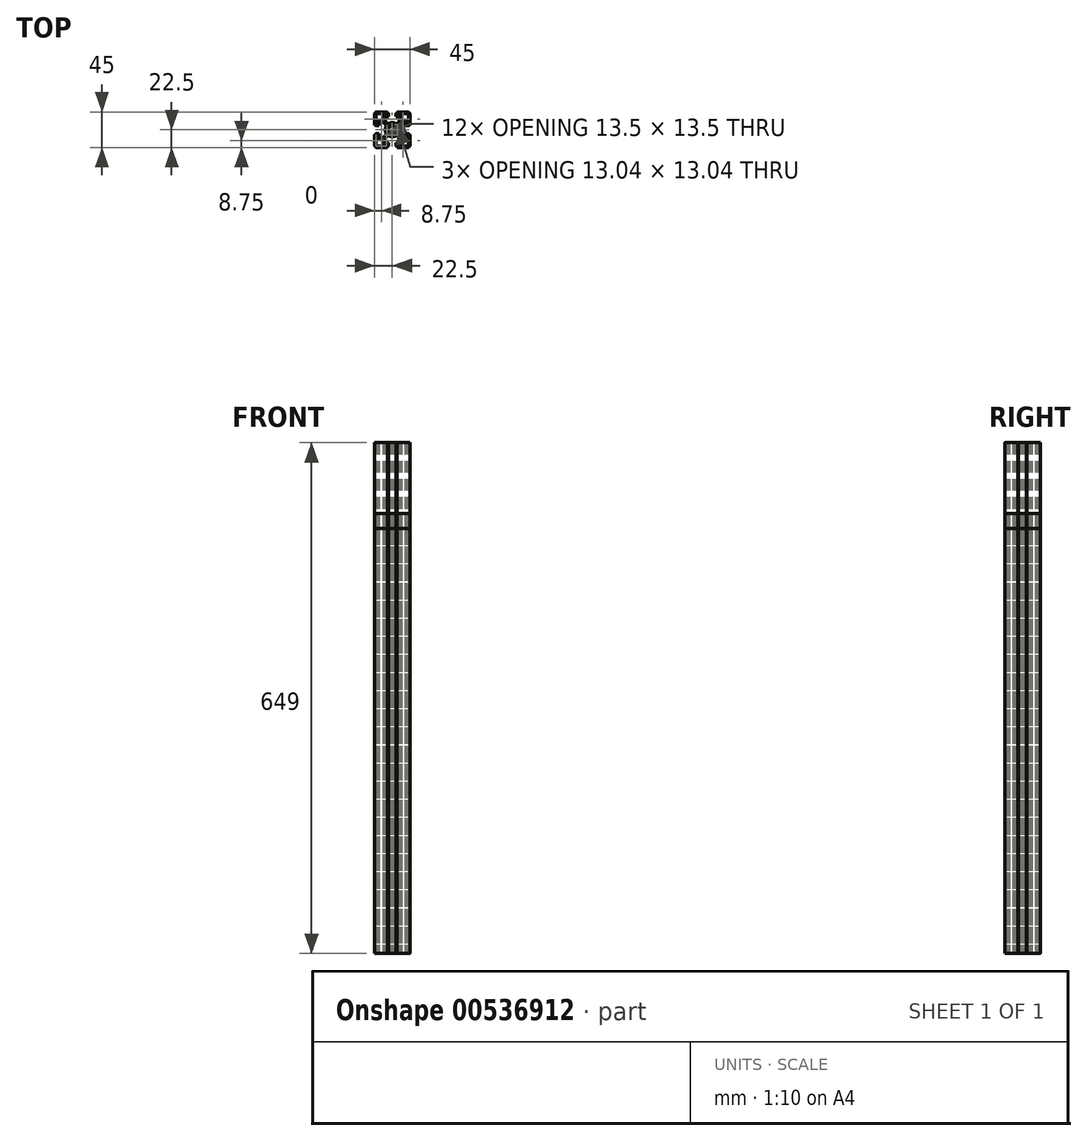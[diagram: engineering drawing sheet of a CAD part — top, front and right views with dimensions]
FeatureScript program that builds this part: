
annotation { "Feature Type Name" : "Feature", "Feature Type Description" : "" }
export const myFeature = defineFeature(function(context is Context, id is Id, definition is map)
    precondition{}
    {
        {
            var Q0;
            Q0=qCreatedBy(makeId("Top.planeOp"),FACE);
            var sketch = newSketch(context, id + "F0", { "sketchPlane" : qUnion([Q0])});
            skLineSegment(sketch, "E0.0.0", {"start": v(5, -21) * mm, "end": v(5, -16.5) * mm});
            skLineSegment(sketch, "E0.0.1", {"start": v(5, -16.5) * mm, "end": v(10, -16.5) * mm});
            skLineSegment(sketch, "E0.0.2", {"start": v(10, -16.5) * mm, "end": v(10, -11.98) * mm});
            skLineSegment(sketch, "E0.0.3", {"start": v(10, -11.98) * mm, "end": v(5.3, -7.28) * mm});
            skArc(sketch, "E0.0.4", {"start": v(5.3, -7.28) * mm, "mid": v(0, -9) * mm, "end": v(-5.3, -7.28) * mm});
            skLineSegment(sketch, "E0.0.5", {"start": v(-5.3, -7.28) * mm, "end": v(-10, -11.98) * mm});
            skLineSegment(sketch, "E0.0.6", {"start": v(-10, -11.98) * mm, "end": v(-10, -16.5) * mm});
            skLineSegment(sketch, "E0.0.7", {"start": v(-10, -16.5) * mm, "end": v(-5, -16.5) * mm});
            skLineSegment(sketch, "E0.0.8", {"start": v(-5, -16.5) * mm, "end": v(-5, -21) * mm});
            skLineSegment(sketch, "E0.0.9", {"start": v(-5, -21) * mm, "end": v(-6, -21) * mm});
            skLineSegment(sketch, "E0.0.10", {"start": v(-6, -21) * mm, "end": v(-6, -22.5) * mm});
            skLineSegment(sketch, "E0.0.11", {"start": v(-6, -22.5) * mm, "end": v(-19.5, -22.5) * mm});
            skArc(sketch, "E0.0.12", {"start": v(-19.5, -22.5) * mm, "mid": v(-21.62, -21.62) * mm, "end": v(-22.5, -19.5) * mm});
            skLineSegment(sketch, "E0.0.13", {"start": v(-22.5, -19.5) * mm, "end": v(-22.5, -6) * mm});
            skLineSegment(sketch, "E0.0.14", {"start": v(-22.5, -6) * mm, "end": v(-21, -6) * mm});
            skLineSegment(sketch, "E0.0.15", {"start": v(-21, -6) * mm, "end": v(-21, -5) * mm});
            skLineSegment(sketch, "E0.0.16", {"start": v(-21, -5) * mm, "end": v(-16.5, -5) * mm});
            skLineSegment(sketch, "E0.0.17", {"start": v(-16.5, -5) * mm, "end": v(-16.5, -10) * mm});
            skLineSegment(sketch, "E0.0.18", {"start": v(-16.5, -10) * mm, "end": v(-11.98, -10) * mm});
            skLineSegment(sketch, "E0.0.19", {"start": v(-11.98, -10) * mm, "end": v(-7.28, -5.3) * mm});
            skArc(sketch, "E0.0.20", {"start": v(-7.28, -5.3) * mm, "mid": v(-9, 0) * mm, "end": v(-7.28, 5.3) * mm});
            skLineSegment(sketch, "E0.0.21", {"start": v(-7.28, 5.3) * mm, "end": v(-11.98, 10) * mm});
            skLineSegment(sketch, "E0.0.22", {"start": v(-11.98, 10) * mm, "end": v(-16.5, 10) * mm});
            skLineSegment(sketch, "E0.0.23", {"start": v(-16.5, 10) * mm, "end": v(-16.5, 5) * mm});
            skLineSegment(sketch, "E0.0.24", {"start": v(-16.5, 5) * mm, "end": v(-21, 5) * mm});
            skLineSegment(sketch, "E0.0.25", {"start": v(-21, 5) * mm, "end": v(-21, 6) * mm});
            skLineSegment(sketch, "E0.0.26", {"start": v(-21, 6) * mm, "end": v(-22.5, 6) * mm});
            skLineSegment(sketch, "E0.0.27", {"start": v(-22.5, 6) * mm, "end": v(-22.5, 19.5) * mm});
            skArc(sketch, "E0.0.28", {"start": v(-22.5, 19.5) * mm, "mid": v(-21.62, 21.62) * mm, "end": v(-19.5, 22.5) * mm});
            skLineSegment(sketch, "E0.0.29", {"start": v(-19.5, 22.5) * mm, "end": v(-6, 22.5) * mm});
            skLineSegment(sketch, "E0.0.30", {"start": v(-6, 22.5) * mm, "end": v(-6, 21) * mm});
            skLineSegment(sketch, "E0.0.31", {"start": v(-6, 21) * mm, "end": v(-5, 21) * mm});
            skLineSegment(sketch, "E0.0.32", {"start": v(-5, 21) * mm, "end": v(-5, 16.5) * mm});
            skLineSegment(sketch, "E0.0.33", {"start": v(-5, 16.5) * mm, "end": v(-10, 16.5) * mm});
            skLineSegment(sketch, "E0.0.34", {"start": v(-10, 16.5) * mm, "end": v(-10, 11.98) * mm});
            skLineSegment(sketch, "E0.0.35", {"start": v(-10, 11.98) * mm, "end": v(-5.3, 7.28) * mm});
            skArc(sketch, "E0.0.36", {"start": v(-5.3, 7.28) * mm, "mid": v(0, 9) * mm, "end": v(5.3, 7.28) * mm});
            skLineSegment(sketch, "E0.0.37", {"start": v(5.3, 7.28) * mm, "end": v(10, 11.98) * mm});
            skLineSegment(sketch, "E0.0.38", {"start": v(10, 11.98) * mm, "end": v(10, 16.5) * mm});
            skLineSegment(sketch, "E0.0.39", {"start": v(10, 16.5) * mm, "end": v(5, 16.5) * mm});
            skLineSegment(sketch, "E0.0.40", {"start": v(5, 16.5) * mm, "end": v(5, 21) * mm});
            skLineSegment(sketch, "E0.0.41", {"start": v(5, 21) * mm, "end": v(6, 21) * mm});
            skLineSegment(sketch, "E0.0.42", {"start": v(6, 21) * mm, "end": v(6, 22.5) * mm});
            skLineSegment(sketch, "E0.0.43", {"start": v(6, 22.5) * mm, "end": v(19.5, 22.5) * mm});
            skArc(sketch, "E0.0.44", {"start": v(19.5, 22.5) * mm, "mid": v(21.62, 21.62) * mm, "end": v(22.5, 19.5) * mm});
            skLineSegment(sketch, "E0.0.45", {"start": v(22.5, 19.5) * mm, "end": v(22.5, 6) * mm});
            skLineSegment(sketch, "E0.0.46", {"start": v(22.5, 6) * mm, "end": v(21, 6) * mm});
            skLineSegment(sketch, "E0.0.47", {"start": v(21, 6) * mm, "end": v(21, 5) * mm});
            skLineSegment(sketch, "E0.0.48", {"start": v(21, 5) * mm, "end": v(16.5, 5) * mm});
            skLineSegment(sketch, "E0.0.49", {"start": v(16.5, 5) * mm, "end": v(16.5, 10) * mm});
            skLineSegment(sketch, "E0.0.50", {"start": v(16.5, 10) * mm, "end": v(11.98, 10) * mm});
            skLineSegment(sketch, "E0.0.51", {"start": v(11.98, 10) * mm, "end": v(7.28, 5.3) * mm});
            skArc(sketch, "E0.0.52", {"start": v(7.28, 5.3) * mm, "mid": v(9, 0) * mm, "end": v(7.28, -5.3) * mm});
            skLineSegment(sketch, "E0.0.53", {"start": v(7.28, -5.3) * mm, "end": v(11.98, -10) * mm});
            skLineSegment(sketch, "E0.0.54", {"start": v(11.98, -10) * mm, "end": v(16.5, -10) * mm});
            skLineSegment(sketch, "E0.0.55", {"start": v(16.5, -10) * mm, "end": v(16.5, -5) * mm});
            skLineSegment(sketch, "E0.0.56", {"start": v(16.5, -5) * mm, "end": v(21, -5) * mm});
            skLineSegment(sketch, "E0.0.57", {"start": v(21, -5) * mm, "end": v(21, -6) * mm});
            skLineSegment(sketch, "E0.0.58", {"start": v(21, -6) * mm, "end": v(22.5, -6) * mm});
            skLineSegment(sketch, "E0.0.59", {"start": v(22.5, -6) * mm, "end": v(22.5, -19.5) * mm});
            skArc(sketch, "E0.0.60", {"start": v(22.5, -19.5) * mm, "mid": v(21.62, -21.62) * mm, "end": v(19.5, -22.5) * mm});
            skLineSegment(sketch, "E0.0.61", {"start": v(19.5, -22.5) * mm, "end": v(6, -22.5) * mm});
            skLineSegment(sketch, "E0.0.62", {"start": v(6, -22.5) * mm, "end": v(6, -21) * mm});
            skLineSegment(sketch, "E0.0.63", {"start": v(6, -21) * mm, "end": v(5, -21) * mm});
            skLineSegment(sketch, "E1.0", {"start": v(11.98, 11.98) * mm, "end": v(18.5, 11.98) * mm});
            skLineSegment(sketch, "E1.1", {"start": v(18.5, 11.98) * mm, "end": v(18.5, 7) * mm});
            skLineSegment(sketch, "E1.2", {"start": v(18.5, 7) * mm, "end": v(20.5, 7) * mm});
            skLineSegment(sketch, "E1.3", {"start": v(20.5, 7) * mm, "end": v(20.5, 20.5) * mm});
            skLineSegment(sketch, "E1.4", {"start": v(20.5, 20.5) * mm, "end": v(7, 20.5) * mm});
            skLineSegment(sketch, "E1.5", {"start": v(7, 20.5) * mm, "end": v(7, 18.5) * mm});
            skLineSegment(sketch, "E1.6", {"start": v(7, 18.5) * mm, "end": v(11.98, 18.5) * mm});
            skLineSegment(sketch, "E1.7", {"start": v(11.98, 18.5) * mm, "end": v(11.98, 11.98) * mm});
            skPoint(sketch, "E1.8", {"position": v(18.5, 9.5) * mm});
            skLineSegment(sketch, "E2.0", {"start": v(-7, 20.5) * mm, "end": v(-20.5, 20.5) * mm});
            skLineSegment(sketch, "E2.1", {"start": v(-7, 18.5) * mm, "end": v(-7, 20.5) * mm});
            skLineSegment(sketch, "E2.2", {"start": v(-11.98, 18.5) * mm, "end": v(-7, 18.5) * mm});
            skLineSegment(sketch, "E2.3", {"start": v(-11.98, 11.98) * mm, "end": v(-11.98, 18.5) * mm});
            skLineSegment(sketch, "E2.4", {"start": v(-18.5, 11.98) * mm, "end": v(-11.98, 11.98) * mm});
            skLineSegment(sketch, "E2.5", {"start": v(-18.5, 7) * mm, "end": v(-18.5, 11.98) * mm});
            skLineSegment(sketch, "E2.6", {"start": v(-20.5, 7) * mm, "end": v(-18.5, 7) * mm});
            skLineSegment(sketch, "E2.7", {"start": v(-20.5, 20.5) * mm, "end": v(-20.5, 7) * mm});
            skPoint(sketch, "E2.8", {"position": v(-19.5, 7) * mm});
            skLineSegment(sketch, "E3.0", {"start": v(-11.98, -11.98) * mm, "end": v(-18.5, -11.98) * mm});
            skLineSegment(sketch, "E3.1", {"start": v(-11.98, -18.5) * mm, "end": v(-11.98, -11.98) * mm});
            skLineSegment(sketch, "E3.2", {"start": v(-7, -18.5) * mm, "end": v(-11.98, -18.5) * mm});
            skLineSegment(sketch, "E3.3", {"start": v(-7, -20.5) * mm, "end": v(-7, -18.5) * mm});
            skLineSegment(sketch, "E3.4", {"start": v(-20.5, -20.5) * mm, "end": v(-7, -20.5) * mm});
            skLineSegment(sketch, "E3.5", {"start": v(-20.5, -7) * mm, "end": v(-20.5, -20.5) * mm});
            skLineSegment(sketch, "E3.6", {"start": v(-18.5, -7) * mm, "end": v(-20.5, -7) * mm});
            skLineSegment(sketch, "E3.7", {"start": v(-18.5, -11.98) * mm, "end": v(-18.5, -7) * mm});
            skLineSegment(sketch, "E4.0", {"start": v(18.5, -11.98) * mm, "end": v(11.98, -11.98) * mm});
            skLineSegment(sketch, "E4.1", {"start": v(18.5, -7) * mm, "end": v(18.5, -11.98) * mm});
            skLineSegment(sketch, "E4.2", {"start": v(20.5, -7) * mm, "end": v(18.5, -7) * mm});
            skLineSegment(sketch, "E4.3", {"start": v(20.5, -20.5) * mm, "end": v(20.5, -7) * mm});
            skLineSegment(sketch, "E4.4", {"start": v(11.98, -11.98) * mm, "end": v(11.98, -18.5) * mm});
            skLineSegment(sketch, "E4.5", {"start": v(11.98, -18.5) * mm, "end": v(7, -18.5) * mm});
            skLineSegment(sketch, "E4.6", {"start": v(7, -18.5) * mm, "end": v(7, -20.5) * mm});
            skLineSegment(sketch, "E4.7", {"start": v(7, -20.5) * mm, "end": v(20.5, -20.5) * mm});
            skPoint(sketch, "E4.8", {"position": v(7, -19.5) * mm});
            skArc(sketch, "E5.1", {"start": v(2.9, 4.08) * mm, "mid": v(1.87, 4.64) * mm, "end": v(0.75, 4.94) * mm});
            skLineSegment(sketch, "E5.2", {"start": v(4.64, 6.52) * mm, "end": v(2.9, 4.08) * mm});
            skArc(sketch, "E5.3", {"start": v(6.52, 4.64) * mm, "mid": v(5.66, 5.66) * mm, "end": v(4.64, 6.52) * mm});
            skLineSegment(sketch, "E5.4", {"start": v(4.08, 2.9) * mm, "end": v(6.52, 4.64) * mm});
            skArc(sketch, "E5.5", {"start": v(4.94, 0.75) * mm, "mid": v(4.64, 1.87) * mm, "end": v(4.08, 2.9) * mm});
            skLineSegment(sketch, "E5.6", {"start": v(5.93, 0.9) * mm, "end": v(4.94, 0.75) * mm});
            skArc(sketch, "E5.7", {"start": v(5.93, -0.9) * mm, "mid": v(6, 0) * mm, "end": v(5.93, 0.9) * mm});
            skLineSegment(sketch, "E5.8", {"start": v(4.94, -0.75) * mm, "end": v(5.93, -0.9) * mm});
            skArc(sketch, "E5.9", {"start": v(4.08, -2.9) * mm, "mid": v(4.64, -1.87) * mm, "end": v(4.94, -0.75) * mm});
            skLineSegment(sketch, "E5.10", {"start": v(6.52, -4.64) * mm, "end": v(4.08, -2.9) * mm});
            skArc(sketch, "E5.11", {"start": v(4.64, -6.52) * mm, "mid": v(5.66, -5.66) * mm, "end": v(6.52, -4.64) * mm});
            skLineSegment(sketch, "E5.12", {"start": v(2.9, -4.08) * mm, "end": v(4.64, -6.52) * mm});
            skArc(sketch, "E5.13", {"start": v(0.75, -4.94) * mm, "mid": v(1.87, -4.64) * mm, "end": v(2.9, -4.08) * mm});
            skLineSegment(sketch, "E5.14", {"start": v(0.9, -5.93) * mm, "end": v(0.75, -4.94) * mm});
            skArc(sketch, "E5.15", {"start": v(-0.9, -5.93) * mm, "mid": v(0, -6) * mm, "end": v(0.9, -5.93) * mm});
            skLineSegment(sketch, "E5.16", {"start": v(-0.75, -4.94) * mm, "end": v(-0.9, -5.93) * mm});
            skArc(sketch, "E5.17", {"start": v(-2.9, -4.08) * mm, "mid": v(-1.87, -4.64) * mm, "end": v(-0.75, -4.94) * mm});
            skLineSegment(sketch, "E5.18", {"start": v(-4.64, -6.52) * mm, "end": v(-2.9, -4.08) * mm});
            skArc(sketch, "E5.19", {"start": v(-6.52, -4.64) * mm, "mid": v(-5.66, -5.66) * mm, "end": v(-4.64, -6.52) * mm});
            skLineSegment(sketch, "E5.20", {"start": v(-4.08, -2.9) * mm, "end": v(-6.52, -4.64) * mm});
            skArc(sketch, "E5.21", {"start": v(-4.94, -0.75) * mm, "mid": v(-4.64, -1.87) * mm, "end": v(-4.08, -2.9) * mm});
            skLineSegment(sketch, "E5.22", {"start": v(-5.93, -0.9) * mm, "end": v(-4.94, -0.75) * mm});
            skArc(sketch, "E5.23", {"start": v(-5.93, 0.9) * mm, "mid": v(-6, 0) * mm, "end": v(-5.93, -0.9) * mm});
            skLineSegment(sketch, "E5.24", {"start": v(-4.94, 0.75) * mm, "end": v(-5.93, 0.9) * mm});
            skArc(sketch, "E5.25", {"start": v(-4.08, 2.9) * mm, "mid": v(-4.64, 1.87) * mm, "end": v(-4.94, 0.75) * mm});
            skLineSegment(sketch, "E5.26", {"start": v(-6.52, 4.64) * mm, "end": v(-4.08, 2.9) * mm});
            skArc(sketch, "E5.27", {"start": v(-4.64, 6.52) * mm, "mid": v(-5.66, 5.66) * mm, "end": v(-6.52, 4.64) * mm});
            skLineSegment(sketch, "E5.28", {"start": v(-2.9, 4.08) * mm, "end": v(-4.64, 6.52) * mm});
            skLineSegment(sketch, "E5.29", {"start": v(-0.9, 5.93) * mm, "end": v(-0.75, 4.94) * mm});
            skArc(sketch, "E5.30", {"start": v(-0.75, 4.94) * mm, "mid": v(-1.87, 4.64) * mm, "end": v(-2.9, 4.08) * mm});
            skArc(sketch, "E5.31", {"start": v(0.9, 5.93) * mm, "mid": v(0, 6) * mm, "end": v(-0.9, 5.93) * mm});
            skLineSegment(sketch, "E5.32", {"start": v(0.75, 4.94) * mm, "end": v(0.9, 5.93) * mm});
            skPoint(sketch, "E5.33", {"position": v(3.77, 5.3) * mm});
            skPoint(sketch, "E5.34", {"position": v(3.77, -5.3) * mm});
            skSolve(sketch);
        }
        {
            var Q0;
            Q0=makeQuery(id+"F0.imprint","IMPRINT",FACE,{"disambiguationData":[TD([[makeQuery(id+"F0.imprint","IMPRINT",EDGE,{"derivedFrom":sQuery(id+"F0.wireOp",EDGE,"E0.0.0")}),-1.0]])]});
            extrude(context, id + "F1", {"entities" : qUnion([Q0]), "depth" : 540 * mm, "offsetDistance" : 25 * mm});
        }
        {
            var Q0;
            Q0 = qSketchRegion(id + "F0", true);
            extrude(context, id + "F2", {"entities" : qUnion([Q0]), "depth" : 649 * mm, "offsetDistance" : 25 * mm});
        }
        {
            var Q0;
            Q0 = qSketchRegion(id + "F0", true);
            extrude(context, id + "F3", {"entities" : qUnion([Q0]), "depth" : 559 * mm, "offsetDistance" : 25 * mm});
        }
    });
